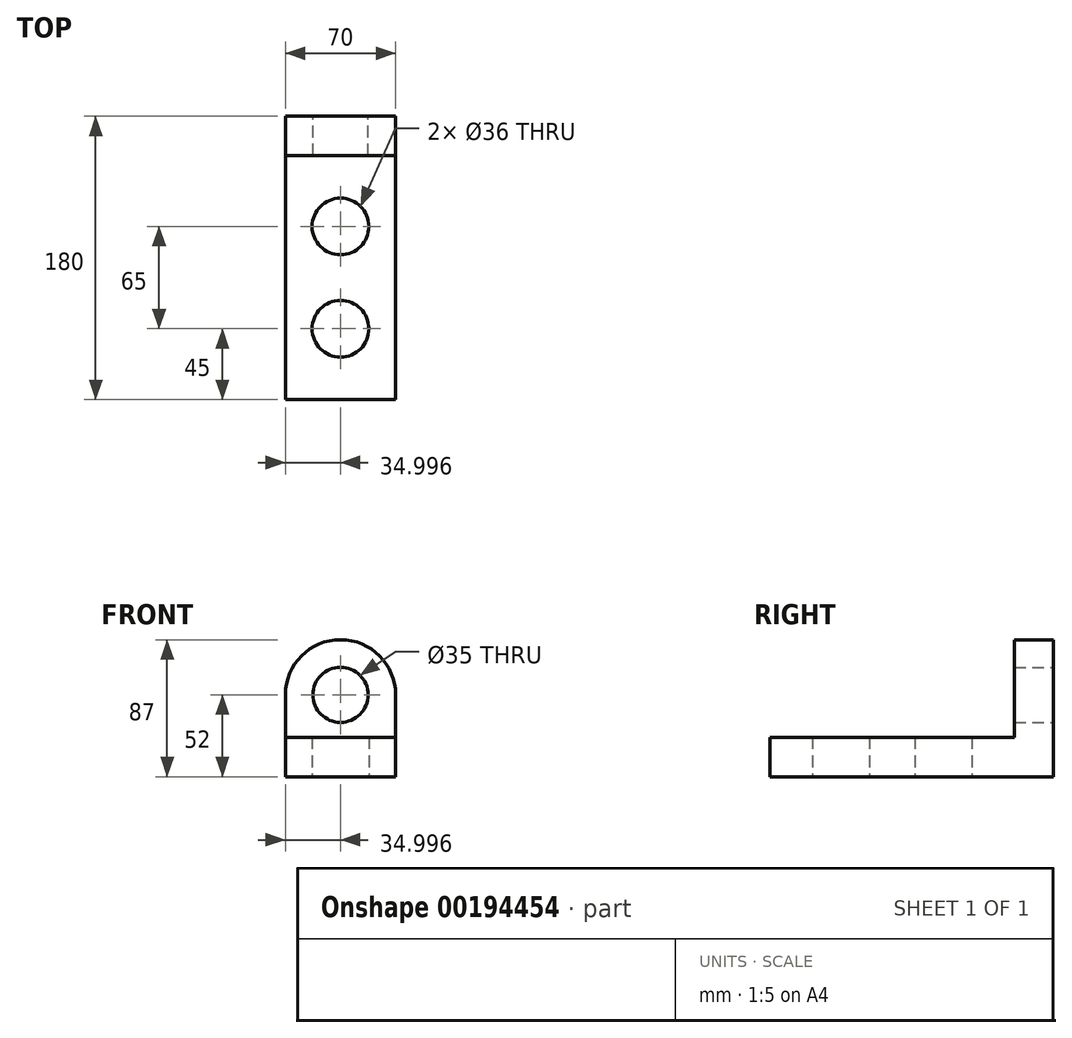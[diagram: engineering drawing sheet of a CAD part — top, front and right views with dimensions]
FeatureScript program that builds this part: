
annotation { "Feature Type Name" : "Feature", "Feature Type Description" : "" }
export const myFeature = defineFeature(function(context is Context, id is Id, definition is map)
    precondition{}
    {
        {
            var Q0;
            Q0=qCreatedBy(makeId("Front.planeOp"),FACE);
            var sketch = newSketch(context, id + "F0", { "sketchPlane" : qUnion([Q0])});
            skLineSegment(sketch, "E0.bottom", {"start": v(-40.44, 0) * mm, "end": v(29.56, 0) * mm});
            skLineSegment(sketch, "E0.top", {"start": v(-40.44, 52) * mm, "end": v(29.56, 52) * mm});
            skLineSegment(sketch, "E0.left", {"start": v(-40.44, 0) * mm, "end": v(-40.44, 52) * mm});
            skLineSegment(sketch, "E0.right", {"start": v(29.56, 0) * mm, "end": v(29.56, 52) * mm});
            skSolve(sketch);
        }
        {
            var Q0;
            Q0 = qSketchRegion(id + "F0", true);
            extrude(context, id + "F1", {"entities" : qUnion([Q0]), "depth" : 180 * mm});
        }
        {
            var Q0;
            Q0=makeQuery(id+"F1.opExtrude","SWEPT_FACE",FACE,{"disambiguationData":[OSD([sQuery(id+"F0.wireOp",EDGE,"E0.top")])]});
            var sketch = newSketch(context, id + "F2", { "sketchPlane" : qUnion([Q0])});
            skLineSegment(sketch, "E1.bottom", {"start": v(-40.44, -25) * mm, "end": v(29.56, -25) * mm});
            skLineSegment(sketch, "E1.top", {"start": v(-40.44, -180) * mm, "end": v(29.56, -180) * mm});
            skLineSegment(sketch, "E1.left", {"start": v(-40.44, -25) * mm, "end": v(-40.44, -180) * mm});
            skLineSegment(sketch, "E1.right", {"start": v(29.56, -25) * mm, "end": v(29.56, -180) * mm});
            skSolve(sketch);
        }
        {
            var Q0;
            Q0 = qSketchRegion(id + "F2", true);
            extrude(context, id + "F3", {"entities" : qUnion([Q0]), "operationType" : NewBodyOperationType.REMOVE, "oppositeDirection" : true, "depth" : 27 * mm});
        }
        {
            var Q0;
            Q0=makeQuery(id+"F1.opExtrude","CAP_FACE",FACE,{"disambiguationData":[OSD([sQuery(id+"F0.wireOp",EDGE,"E0.bottom"),sQuery(id+"F0.wireOp",EDGE,"E0.top"),sQuery(id+"F0.wireOp",EDGE,"E0.left"),sQuery(id+"F0.wireOp",EDGE,"E0.right")])],"isStart":true});
            var sketch = newSketch(context, id + "F4", { "sketchPlane" : qUnion([Q0])});
            skArc(sketch, "E2", {"start": v(40.44, 52) * mm, "mid": v(5.44, 87) * mm, "end": v(-29.56, 52) * mm});
            skPoint(sketch, "E3", {"position": v(40.44, 52) * mm});
            skPoint(sketch, "E4", {"position": v(-29.56, 52) * mm});
            skLineSegment(sketch, "E5", {"start": v(-29.56, 52) * mm, "end": v(40.44, 52) * mm});
            skSolve(sketch);
        }
        {
            var Q0;
            Q0 = qSketchRegion(id + "F4", true);
            var Q1;
            Q1=sQuery(id+"F4.wireOp",EDGE,"E2");
            extrude(context, id + "F5", {"entities" : qUnion([Q0]), "operationType" : NewBodyOperationType.ADD, "surfaceEntities" : qUnion([Q1]), "oppositeDirection" : true, "depth" : 25 * mm});
        }
        {
            var Q0;
            Q0=qCreatedBy(makeId("Front.planeOp"),FACE);
            var sketch = newSketch(context, id + "F6", { "sketchPlane" : qUnion([Q0])});
            skCircle(sketch, "E6", {"center": v(-5.44, 52) * mm, "radius": 17.5 * mm});
            skSolve(sketch);
        }
        {
            var Q0;
            Q0 = qSketchRegion(id + "F6", true);
            extrude(context, id + "F7", {"entities" : qUnion([Q0]), "operationType" : NewBodyOperationType.REMOVE, "depth" : 25 * mm});
        }
        {
            var Q0;
            Q0=qCreatedBy(makeId("Top.planeOp"),FACE);
            var sketch = newSketch(context, id + "F8", { "sketchPlane" : qUnion([Q0])});
            skCircle(sketch, "E7", {"center": v(-5.44, -70) * mm, "radius": 18 * mm});
            skCircle(sketch, "E8", {"center": v(-5.44, -135) * mm, "radius": 18 * mm});
            skSolve(sketch);
        }
        {
            var Q0;
            Q0 = qSketchRegion(id + "F8", true);
            extrude(context, id + "F9", {"entities" : qUnion([Q0]), "operationType" : NewBodyOperationType.REMOVE, "endBound" : BoundingType.THROUGH_ALL, "depth" : 25 * mm});
        }
    });
